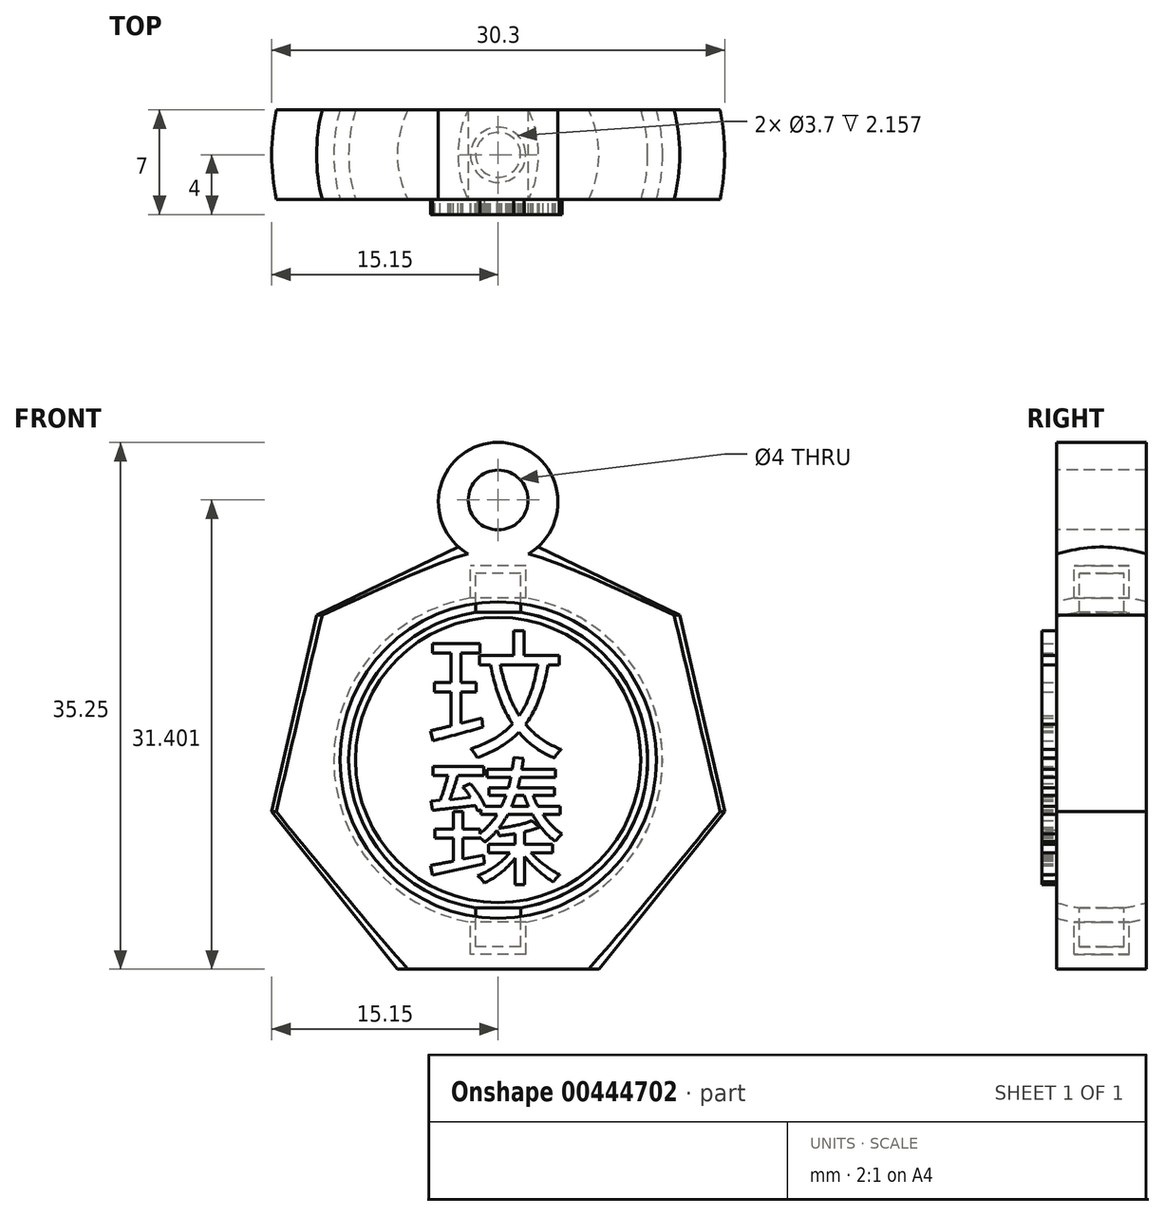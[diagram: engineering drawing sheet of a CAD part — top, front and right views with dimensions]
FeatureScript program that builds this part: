
annotation { "Feature Type Name" : "Feature", "Feature Type Description" : "" }
export const myFeature = defineFeature(function(context is Context, id is Id, definition is map)
    precondition{}
    {
        {
            var Q0;
            Q0=qCreatedBy(makeId("Front.planeOp"),FACE);
            var sketch = newSketch(context, id + "F0", { "sketchPlane" : qUnion([Q0])});
            skLineSegment(sketch, "E0.bottom", {"start": v(1.85, -13) * mm, "end": v(-1.85, -13) * mm});
            skLineSegment(sketch, "E0.top", {"start": v(1.85, 13) * mm, "end": v(-1.85, 13) * mm});
            skLineSegment(sketch, "E0.left", {"start": v(1.85, -13) * mm, "end": v(1.85, 13) * mm});
            skLineSegment(sketch, "E0.right", {"start": v(-1.85, -13) * mm, "end": v(-1.85, 13) * mm});
            skPoint(sketch, "E0.middle", {"position": v(0, 0) * mm});
            skLineSegment(sketch, "E1.bottom", {"start": v(1.5, -12.5) * mm, "end": v(-1.5, -12.5) * mm});
            skLineSegment(sketch, "E1.top", {"start": v(1.5, 12.5) * mm, "end": v(-1.5, 12.5) * mm});
            skLineSegment(sketch, "E1.left", {"start": v(1.5, -12.5) * mm, "end": v(1.5, 12.5) * mm});
            skLineSegment(sketch, "E1.right", {"start": v(-1.5, -12.5) * mm, "end": v(-1.5, 12.5) * mm});
            skCircle(sketch, "E2", {"center": v(0, 0) * mm, "radius": 10 * mm});
            skCircle(sketch, "E3", {"center": v(0, 0) * mm, "radius": 11 * mm});
            skCircle(sketch, "E4.cCircle", {"center": v(0, 0) * mm, "radius": 14 * mm, "construction": true});
            skLineSegment(sketch, "E4.0", {"start": v(15.15, -3.46) * mm, "end": v(6.74, -14) * mm});
            skLineSegment(sketch, "E4.1", {"start": v(6.74, -14) * mm, "end": v(-6.74, -14) * mm});
            skLineSegment(sketch, "E4.2", {"start": v(-6.74, -14) * mm, "end": v(-15.15, -3.46) * mm});
            skLineSegment(sketch, "E4.3", {"start": v(-15.15, -3.46) * mm, "end": v(-12.15, 9.69) * mm});
            skLineSegment(sketch, "E4.4", {"start": v(-12.15, 9.69) * mm, "end": v(0, 15.54) * mm});
            skLineSegment(sketch, "E4.5", {"start": v(0, 15.54) * mm, "end": v(12.15, 9.69) * mm});
            skLineSegment(sketch, "E4.6", {"start": v(12.15, 9.69) * mm, "end": v(15.15, -3.46) * mm});
            skPoint(sketch, "E4.0.midPoint", {"position": v(10.95, -8.73) * mm});
            skSolve(sketch);
        }
        {
            var Q0;
            Q0=qCreatedBy(makeId("Front.planeOp"),FACE);
            var sketch = newSketch(context, id + "F1", { "sketchPlane" : qUnion([Q0])});
            skLineSegment(sketch, "E5.0", {"start": v(-6.74, -14) * mm, "end": v(-15.15, -3.46) * mm});
            skLineSegment(sketch, "E5.1", {"start": v(12.15, 9.69) * mm, "end": v(15.15, -3.46) * mm});
            skLineSegment(sketch, "E5.2", {"start": v(-15.15, -3.46) * mm, "end": v(-12.15, 9.69) * mm});
            skLineSegment(sketch, "E5.3", {"start": v(-12.15, 9.69) * mm, "end": v(0, 15.54) * mm});
            skLineSegment(sketch, "E5.4", {"start": v(1.85, -13) * mm, "end": v(-1.85, -13) * mm});
            skLineSegment(sketch, "E5.5", {"start": v(1.85, 13) * mm, "end": v(-1.85, 13) * mm});
            skLineSegment(sketch, "E5.6", {"start": v(1.85, -13) * mm, "end": v(1.85, -10.84) * mm});
            skLineSegment(sketch, "E5.7", {"start": v(-1.85, -13) * mm, "end": v(-1.85, -10.84) * mm});
            skLineSegment(sketch, "E5.8", {"start": v(1.5, -12.5) * mm, "end": v(-1.5, -12.5) * mm});
            skLineSegment(sketch, "E5.9", {"start": v(1.5, 12.5) * mm, "end": v(-1.5, 12.5) * mm});
            skLineSegment(sketch, "E5.10", {"start": v(1.5, -12.5) * mm, "end": v(1.5, -9.89) * mm});
            skLineSegment(sketch, "E5.11", {"start": v(-1.5, -12.5) * mm, "end": v(-1.5, -9.89) * mm});
            skArc(sketch, "E5.12", {"start": v(-1.5, 9.89) * mm, "mid": v(-10, 0) * mm, "end": v(-1.5, -9.89) * mm});
            skArc(sketch, "E5.13", {"start": v(-1.85, 10.84) * mm, "mid": v(-11, 0) * mm, "end": v(-1.85, -10.84) * mm});
            skLineSegment(sketch, "E5.15", {"start": v(15.15, -3.46) * mm, "end": v(6.74, -14) * mm});
            skLineSegment(sketch, "E5.16", {"start": v(6.74, -14) * mm, "end": v(-6.74, -14) * mm});
            skLineSegment(sketch, "E5.17", {"start": v(0, 15.54) * mm, "end": v(12.15, 9.69) * mm});
            skLineSegment(sketch, "E6.trimOffspring", {"start": v(-1.5, 9.89) * mm, "end": v(-1.5, 12.5) * mm});
            skLineSegment(sketch, "E7.trimOffspring", {"start": v(-1.85, 10.84) * mm, "end": v(-1.85, 13) * mm});
            skLineSegment(sketch, "E8.trimOffspring", {"start": v(1.5, 9.89) * mm, "end": v(1.5, 12.5) * mm});
            skLineSegment(sketch, "E9.trimOffspring", {"start": v(1.85, 10.84) * mm, "end": v(1.85, 13) * mm});
            skArc(sketch, "E10.trimOffspring", {"start": v(1.5, -9.89) * mm, "mid": v(10, 0) * mm, "end": v(1.5, 9.89) * mm});
            skArc(sketch, "E11.trimOffspring", {"start": v(1.85, -10.84) * mm, "mid": v(11, 0) * mm, "end": v(1.85, 10.84) * mm});
            skSolve(sketch);
        }
        {
            var Q0;
            Q0=qCreatedBy(makeId("Front.planeOp"),FACE);
            var sketch = newSketch(context, id + "F2", { "sketchPlane" : qUnion([Q0])});
            skLineSegment(sketch, "E12.0", {"start": v(-6.74, -14) * mm, "end": v(-15.15, -3.46) * mm});
            skLineSegment(sketch, "E12.1", {"start": v(12.15, 9.69) * mm, "end": v(15.15, -3.46) * mm});
            skLineSegment(sketch, "E12.2", {"start": v(-15.15, -3.46) * mm, "end": v(-12.15, 9.69) * mm});
            skLineSegment(sketch, "E12.3", {"start": v(-12.15, 9.69) * mm, "end": v(0, 15.54) * mm});
            skLineSegment(sketch, "E12.4", {"start": v(1.85, -13) * mm, "end": v(-1.85, -13) * mm});
            skLineSegment(sketch, "E12.5", {"start": v(1.85, 13) * mm, "end": v(-1.85, 13) * mm});
            skLineSegment(sketch, "E12.6", {"start": v(1.85, -13) * mm, "end": v(1.85, -10.84) * mm});
            skLineSegment(sketch, "E12.7", {"start": v(-1.85, -13) * mm, "end": v(-1.85, -10.84) * mm});
            skLineSegment(sketch, "E12.8", {"start": v(1.5, -12.5) * mm, "end": v(-1.5, -12.5) * mm});
            skLineSegment(sketch, "E12.9", {"start": v(1.5, 12.5) * mm, "end": v(-1.5, 12.5) * mm});
            skLineSegment(sketch, "E12.10", {"start": v(1.5, -12.5) * mm, "end": v(1.5, -9.89) * mm});
            skLineSegment(sketch, "E12.11", {"start": v(-1.5, -12.5) * mm, "end": v(-1.5, -9.89) * mm});
            skArc(sketch, "E12.12", {"start": v(-1.5, 9.89) * mm, "mid": v(-10, 0) * mm, "end": v(-1.5, -9.89) * mm});
            skArc(sketch, "E12.13", {"start": v(-1.85, 10.84) * mm, "mid": v(-11, 0) * mm, "end": v(-1.85, -10.84) * mm});
            skLineSegment(sketch, "E12.14", {"start": v(15.15, -3.46) * mm, "end": v(6.74, -14) * mm});
            skLineSegment(sketch, "E12.15", {"start": v(6.74, -14) * mm, "end": v(-6.74, -14) * mm});
            skLineSegment(sketch, "E12.16", {"start": v(0, 15.54) * mm, "end": v(12.15, 9.69) * mm});
            skLineSegment(sketch, "E12.17", {"start": v(-1.5, 9.89) * mm, "end": v(-1.5, 12.5) * mm});
            skLineSegment(sketch, "E12.18", {"start": v(-1.85, 10.84) * mm, "end": v(-1.85, 13) * mm});
            skLineSegment(sketch, "E12.19", {"start": v(1.5, 9.89) * mm, "end": v(1.5, 12.5) * mm});
            skLineSegment(sketch, "E12.20", {"start": v(1.85, 10.84) * mm, "end": v(1.85, 13) * mm});
            skArc(sketch, "E12.21", {"start": v(1.5, -9.89) * mm, "mid": v(10, 0) * mm, "end": v(1.5, 9.89) * mm});
            skArc(sketch, "E12.22", {"start": v(1.85, -10.84) * mm, "mid": v(11, 0) * mm, "end": v(1.85, 10.84) * mm});
            skLineSegment(sketch, "E13", {"start": v(0, 15.54) * mm, "end": v(0, -14) * mm});
            skSolve(sketch);
        }
        {
            var Q0;
            Q0=qCreatedBy(makeId("Front.planeOp"),FACE);
            var sketch = newSketch(context, id + "F3", { "sketchPlane" : qUnion([Q0])});
            skLineSegment(sketch, "E14.1", {"start": v(12.15, 9.69) * mm, "end": v(15.15, -3.46) * mm});
            skLineSegment(sketch, "E14.4", {"start": v(1.85, -13) * mm, "end": v(0, -13) * mm});
            skLineSegment(sketch, "E14.5", {"start": v(1.85, 13) * mm, "end": v(0, 13) * mm});
            skLineSegment(sketch, "E14.6", {"start": v(1.85, -13) * mm, "end": v(1.85, -10.84) * mm});
            skLineSegment(sketch, "E14.8", {"start": v(1.5, -12.5) * mm, "end": v(0, -12.5) * mm});
            skLineSegment(sketch, "E14.9", {"start": v(1.5, 12.5) * mm, "end": v(0, 12.5) * mm});
            skLineSegment(sketch, "E14.10", {"start": v(1.5, -12.5) * mm, "end": v(1.5, -9.89) * mm});
            skLineSegment(sketch, "E14.14", {"start": v(15.15, -3.46) * mm, "end": v(6.74, -14) * mm});
            skLineSegment(sketch, "E14.15", {"start": v(6.74, -14) * mm, "end": v(0, -14) * mm});
            skLineSegment(sketch, "E14.16", {"start": v(0, 15.54) * mm, "end": v(12.15, 9.69) * mm});
            skLineSegment(sketch, "E14.19", {"start": v(1.5, 9.89) * mm, "end": v(1.5, 12.5) * mm});
            skLineSegment(sketch, "E14.20", {"start": v(1.85, 10.84) * mm, "end": v(1.85, 13) * mm});
            skArc(sketch, "E14.21", {"start": v(1.5, -9.89) * mm, "mid": v(10, 0) * mm, "end": v(1.5, 9.89) * mm});
            skArc(sketch, "E14.22", {"start": v(1.85, -10.84) * mm, "mid": v(11, 0) * mm, "end": v(1.85, 10.84) * mm});
            skLineSegment(sketch, "E14.23", {"start": v(0, 15.54) * mm, "end": v(0, 13) * mm});
            skPoint(sketch, "E14.3.end.orphan", {"position": v(0, 15.54) * mm});
            skPoint(sketch, "E14.3.start.orphan", {"position": v(-12.15, 9.69) * mm});
            skPoint(sketch, "E14.17.end.orphan", {"position": v(-1.5, 12.5) * mm});
            skPoint(sketch, "E14.17.start.orphan", {"position": v(-1.5, 9.89) * mm});
            skPoint(sketch, "E14.18.end.orphan", {"position": v(-1.85, 13) * mm});
            skPoint(sketch, "E14.18.start.orphan", {"position": v(-1.85, 10.84) * mm});
            skPoint(sketch, "E14.13.end.orphan", {"position": v(-1.85, -10.84) * mm});
            skPoint(sketch, "E14.13.start.orphan", {"position": v(-1.85, 10.84) * mm});
            skPoint(sketch, "E14.12.end.orphan", {"position": v(-1.5, -9.89) * mm});
            skPoint(sketch, "E14.12.start.orphan", {"position": v(-1.5, 9.89) * mm});
            skPoint(sketch, "E14.2.end.orphan", {"position": v(-12.15, 9.69) * mm});
            skPoint(sketch, "E14.2.start.orphan", {"position": v(-15.15, -3.46) * mm});
            skLineSegment(sketch, "E15.trimOffspring", {"start": v(0, 12.5) * mm, "end": v(0, -12.5) * mm});
            skPoint(sketch, "E14.0.end.orphan", {"position": v(-15.15, -3.46) * mm});
            skPoint(sketch, "E14.0.start.orphan", {"position": v(-6.74, -14) * mm});
            skPoint(sketch, "E14.11.end.orphan", {"position": v(-1.5, -9.89) * mm});
            skPoint(sketch, "E14.11.start.orphan", {"position": v(-1.5, -12.5) * mm});
            skPoint(sketch, "E14.7.end.orphan", {"position": v(-1.85, -10.84) * mm});
            skPoint(sketch, "E14.7.start.orphan", {"position": v(-1.85, -13) * mm});
            skLineSegment(sketch, "E16.trimOffspring", {"start": v(0, -13) * mm, "end": v(0, -14) * mm});
            skSolve(sketch);
        }
        {
            var Q0;
            Q0=qSketchRegion(id+"F3",true);
            var Q1;
            Q1=sQuery(id+"F3.wireOp",EDGE,"E15.trimOffspring");
            revolve(context, id + "F4", {"entities" : qUnion([Q0]), "axis" : qUnion([Q1]), "revolveType" : RevolveType.FULL});
        }
        {
            var Q0;
            Q0=qCreatedBy(makeId("Right.planeOp"),FACE);
            var sketch = newSketch(context, id + "F5", { "sketchPlane" : qUnion([Q0])});
            skLineSegment(sketch, "E17.bottom", {"start": v(3, 20.08) * mm, "end": v(25.6, 20.08) * mm});
            skLineSegment(sketch, "E17.top", {"start": v(3, -19.17) * mm, "end": v(25.6, -19.17) * mm});
            skLineSegment(sketch, "E17.left", {"start": v(3, 20.08) * mm, "end": v(3, -19.17) * mm});
            skLineSegment(sketch, "E17.right", {"start": v(25.6, 20.08) * mm, "end": v(25.6, -19.17) * mm});
            skLineSegment(sketch, "E18.MirrorCS", {"start": v(-3, 20.08) * mm, "end": v(-25.6, 20.08) * mm});
            skLineSegment(sketch, "E19.MirrorCS", {"start": v(-3, -19.17) * mm, "end": v(-25.6, -19.17) * mm});
            skLineSegment(sketch, "E20.MirrorCS", {"start": v(-3, 20.08) * mm, "end": v(-3, -19.17) * mm});
            skLineSegment(sketch, "E21.MirrorCS", {"start": v(-25.6, 20.08) * mm, "end": v(-25.6, -19.17) * mm});
            skSolve(sketch);
        }
        {
            var Q0;
            Q0=qSketchRegion(id+"F5",true);
            extrude(context, id + "F6", {"entities" : qUnion([Q0]), "operationType" : NewBodyOperationType.REMOVE, "endBound" : BoundingType.SYMMETRIC, "oppositeDirection" : true, "depth" : 60 * mm});
        }
        {
            var Q0;
            Q0=qCreatedBy(makeId("Front.planeOp"),FACE);
            var sketch = newSketch(context, id + "F7", { "sketchPlane" : qUnion([Q0])});
            skCircle(sketch, "E22", {"center": v(0, 17.25) * mm, "radius": 4 * mm});
            skSolve(sketch);
        }
        {
            var Q0;
            Q0=qSketchRegion(id+"F7",true);
            extrude(context, id + "F8", {"entities" : qUnion([Q0]), "operationType" : NewBodyOperationType.ADD, "endBound" : BoundingType.SYMMETRIC, "depth" : 6 * mm});
        }
        {
            var Q0;
            Q0=qCreatedBy(makeId("Front.planeOp"),FACE);
            var sketch = newSketch(context, id + "F9", { "sketchPlane" : qUnion([Q0])});
            skCircle(sketch, "E23", {"center": v(0, 17.4) * mm, "radius": 2 * mm});
            skSolve(sketch);
        }
        {
            var Q0;
            Q0=qSketchRegion(id+"F9",true);
            extrude(context, id + "F10", {"entities" : qUnion([Q0]), "operationType" : NewBodyOperationType.REMOVE, "endBound" : BoundingType.SYMMETRIC, "oppositeDirection" : true, "depth" : 25 * mm});
        }
        {
            var Q0;
            Q0=makeQuery(id+"F6.boolean.opBoolean","COPY",FACE,{"disambiguationData":[TD([makeQuery(id+"F4.opRevolve","SWEPT_FACE",FACE,{"disambiguationData":[OSD([sQuery(id+"F3.wireOp",EDGE,"E14.21")])]})])],"derivedFrom":makeQuery(id+"F6.opExtrude","SWEPT_FACE",FACE,{"disambiguationData":[OSD([sQuery(id+"F5.wireOp",EDGE,"E20.MirrorCS")])]})});
            var sketch = newSketch(context, id + "F11", { "sketchPlane" : qUnion([Q0])});
            skText(sketch, "E24", { "text": "玟", "fontName": "NotoSansCJKjp-Regular.otf"});
            skText(sketch, "E25", { "text": "臻", "fontName": "NotoSansCJKjp-Regular.otf"});
            const initialGuessF11  = {"E24": [-0.00486, 0.00086, 1, 0, 0.00674], "E25": [-0.00482, -0.00766, 1, 0, 0.00674]};
            skSetInitialGuess(sketch, initialGuessF11);
            skSolve(sketch);
        }
        {
            var Q0;
            Q0 = qSketchRegion(id + "F11", true);
            extrude(context, id + "F12", {"entities" : qUnion([Q0]), "operationType" : NewBodyOperationType.ADD, "depth" : 1 * mm});
        }
    });
